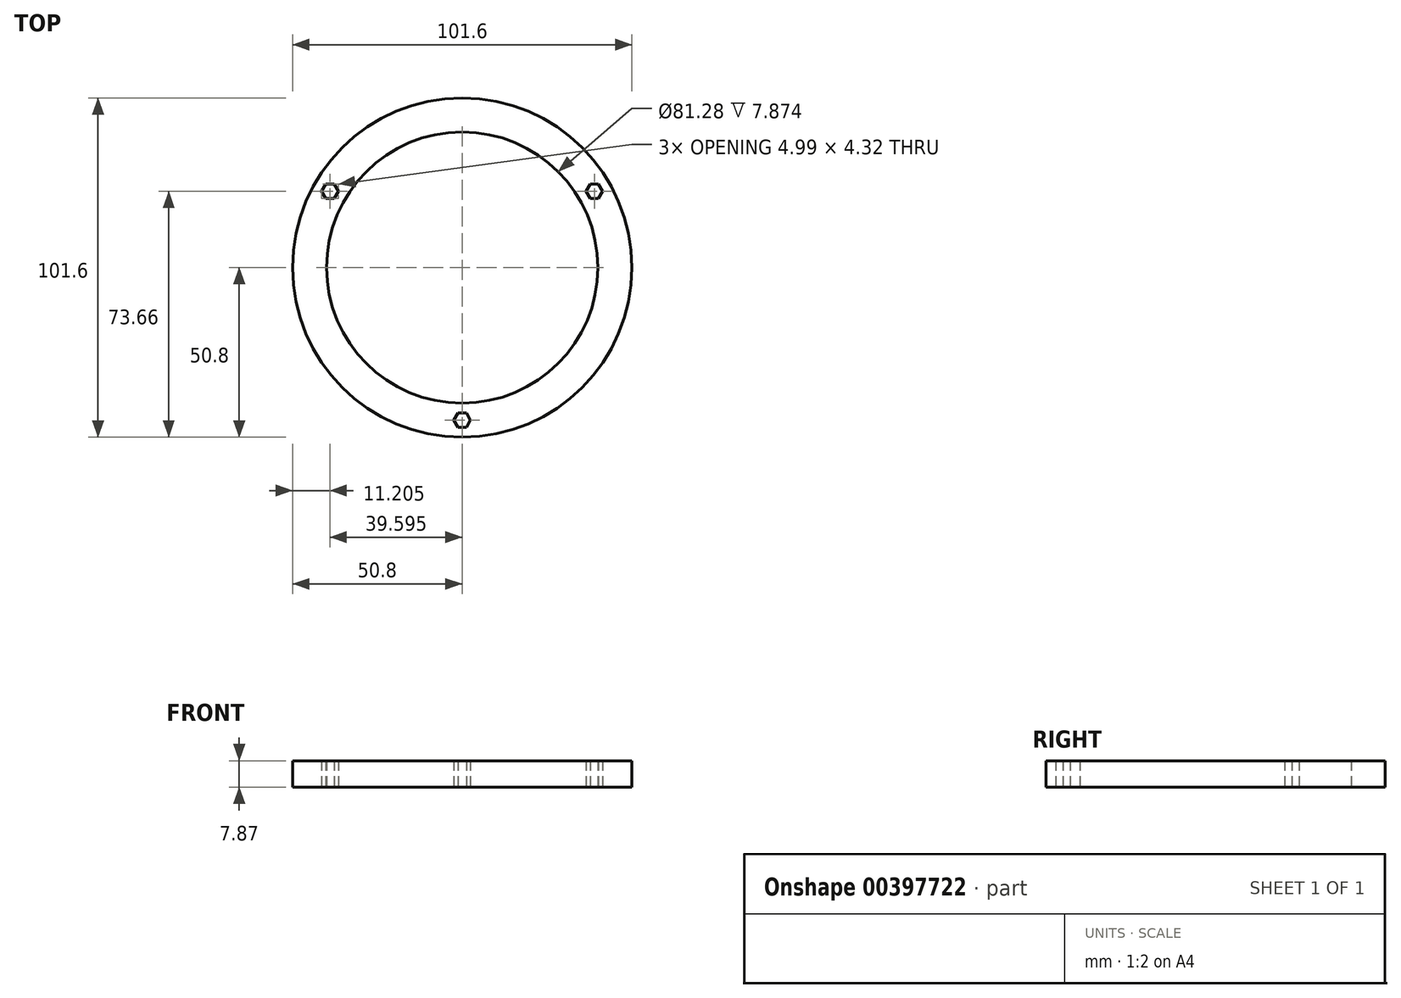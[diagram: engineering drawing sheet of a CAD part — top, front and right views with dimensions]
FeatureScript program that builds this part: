
annotation { "Feature Type Name" : "Feature", "Feature Type Description" : "" }
export const myFeature = defineFeature(function(context is Context, id is Id, definition is map)
    precondition{}
    {
        {
            var Q0;
            Q0=qCreatedBy(makeId("Top.planeOp"),FACE);
            var sketch = newSketch(context, id + "F0", { "sketchPlane" : qUnion([Q0])});
            skCircle(sketch, "E0", {"center": v(0, 0) * mm, "radius": 50.8 * mm});
            skCircle(sketch, "E1", {"center": v(0, 0) * mm, "radius": 40.64 * mm});
            skLineSegment(sketch, "E2", {"start": v(0, 0) * mm, "end": v(0, -45.72) * mm, "construction": true});
            skLineSegment(sketch, "E3", {"start": v(0, 0) * mm, "end": v(39.6, 22.86) * mm, "construction": true});
            skLineSegment(sketch, "E4", {"start": v(0, 0) * mm, "end": v(-39.6, 22.86) * mm, "construction": true});
            skCircle(sketch, "E5.cCircle", {"center": v(-39.6, 22.86) * mm, "radius": 2.16 * mm, "construction": true});
            skLineSegment(sketch, "E5.0", {"start": v(-40.84, 25.02) * mm, "end": v(-38.35, 25.02) * mm});
            skLineSegment(sketch, "E5.1", {"start": v(-38.35, 25.02) * mm, "end": v(-37.1, 22.86) * mm});
            skLineSegment(sketch, "E5.2", {"start": v(-37.1, 22.86) * mm, "end": v(-38.35, 20.7) * mm});
            skLineSegment(sketch, "E5.3", {"start": v(-38.35, 20.7) * mm, "end": v(-40.84, 20.7) * mm});
            skLineSegment(sketch, "E5.4", {"start": v(-40.84, 20.7) * mm, "end": v(-42.09, 22.86) * mm});
            skLineSegment(sketch, "E5.5", {"start": v(-42.09, 22.86) * mm, "end": v(-40.84, 25.02) * mm});
            skPoint(sketch, "E5.0.midPoint", {"position": v(-39.6, 25.02) * mm});
            skCircle(sketch, "E6.cCircle", {"center": v(39.6, 22.86) * mm, "radius": 2.16 * mm, "construction": true});
            skLineSegment(sketch, "E6.0", {"start": v(38.35, 25.02) * mm, "end": v(40.84, 25.02) * mm});
            skLineSegment(sketch, "E6.1", {"start": v(40.84, 25.02) * mm, "end": v(42.09, 22.86) * mm});
            skLineSegment(sketch, "E6.2", {"start": v(42.09, 22.86) * mm, "end": v(40.84, 20.7) * mm});
            skLineSegment(sketch, "E6.3", {"start": v(40.84, 20.7) * mm, "end": v(38.35, 20.7) * mm});
            skLineSegment(sketch, "E6.4", {"start": v(38.35, 20.7) * mm, "end": v(37.1, 22.86) * mm});
            skLineSegment(sketch, "E6.5", {"start": v(37.1, 22.86) * mm, "end": v(38.35, 25.02) * mm});
            skPoint(sketch, "E6.0.midPoint", {"position": v(39.6, 25.02) * mm});
            skCircle(sketch, "E7.cCircle", {"center": v(0, -45.72) * mm, "radius": 2.16 * mm, "construction": true});
            skLineSegment(sketch, "E7.0", {"start": v(1.25, -47.88) * mm, "end": v(-1.25, -47.88) * mm});
            skLineSegment(sketch, "E7.1", {"start": v(-1.25, -47.88) * mm, "end": v(-2.5, -45.72) * mm});
            skLineSegment(sketch, "E7.2", {"start": v(-2.5, -45.72) * mm, "end": v(-1.25, -43.56) * mm});
            skLineSegment(sketch, "E7.3", {"start": v(-1.25, -43.56) * mm, "end": v(1.25, -43.56) * mm});
            skLineSegment(sketch, "E7.4", {"start": v(1.25, -43.56) * mm, "end": v(2.5, -45.72) * mm});
            skLineSegment(sketch, "E7.5", {"start": v(2.5, -45.72) * mm, "end": v(1.25, -47.88) * mm});
            skPoint(sketch, "E7.0.midPoint", {"position": v(0, -47.88) * mm});
            skSolve(sketch);
        }
        {
            var Q0;
            Q0=makeQuery(id+"F0.imprint","IMPRINT",FACE,{"disambiguationData":[TD([[makeQuery(id+"F0.imprint","IMPRINT",EDGE,{"derivedFrom":sQuery(id+"F0.wireOp",EDGE,"E0")}),1.0]])]});
            extrude(context, id + "F1", {"entities" : qUnion([Q0]), "depth" : 7.87 * mm});
        }
    });
